# Revit family: Chaine de traitement par Absorption (support au sol) - AD5130
name_source: partatom
category: Equipement spécialisé
revit_build: Autodesk Revit 2018 (Build: 20170223_1515(x64)
units: mm (PartAtom-declared; Revit-internal decimal feet)

## family parameters
Basée sur le plan de construction = Non
Cote de connecteur circulaire = Utiliser le diamètre
Couper avec des vides une fois chargée = Non
Partagée = Non
Point de calcul de pièce = Non
Toujours verticalement = Oui
Type d'élément = Normal

## types (1)
- SEC 7 HC - AD 5130
    COS_PHI = 0.9
    DEBIT_ENTREE_AIR = 129.0 m³/h
    DEBIT_SORTIE_AIR = 129.0 m³/h
    DESCR_ALIM_X = Alimentation X ; ID 3G1mm² ;
    DESCR_ENTREE_AIR = Entrée Air ; 129 m3/h à 10 bar ; ID G 3/4" ;
    DESCR_SORTIE_AIR = Sortie Air ; 129 m3/h à 10 bar ; ID G 1/2" ;
    DIAM_ENTREE_AIR = 20 mm  [stored 0.0656168 ft]
    DIAM_SORTIE_AIR = 15 mm  [stored 0.0492126 ft]
    Diametre_Percement_1 = 11 mm  [stored 0.0360892 ft]
    Diametre_Percement_2 = 14 mm  [stored 0.0459318 ft]
    Diametre_Percement_3 = 25 mm  [stored 0.082021 ft]
    Entraxe_Horizontal_Percement_1 = 410 mm  [stored 1.34514 ft]
    Entraxe_Horizontal_Percement_2 = 410 mm  [stored 1.34514 ft]
    Entraxe_Rouleau = 313 mm  [stored 1.0269 ft]
    Entraxe_Vertical_Percement_1 = 400 mm  [stored 1.31234 ft]
    Entraxe_Vertical_Percement_2 = 150 mm
    FREQUENCE = 50 Hz
    Fabricant = MIL'S
    HAUTEUR = 1570 mm
    Hauteur_Boitier_Commande = 1050 mm
    Hauteur_Detente = 1470 mm
    Hauteur_Filtres = 800 mm  [stored 2.62467 ft]
    Hauteur_Rouleau = 20 mm  [stored 0.0656168 ft]
    Hauteur_Support = 1570 mm
    Hauteur_Vidange = 50 mm  [stored 0.164042 ft]
    LARGEUR = 460 mm  [stored 1.50919 ft]
    LONGUEUR = 250 mm  [stored 0.82021 ft]
    Largeur_Support = 460 mm  [stored 1.50919 ft]
    Lien espace client = https://www.mils.fr
    Longueur_Rouleau = 1480 mm  [stored 4.85564 ft]
    Modèle = SEC HC - AD 5130
    NBR_POLES = 1
    NEUTRE = Oui
    POIDS(Kg) = 100 mm  [stored 0.328084 ft]
    PUISS_APPARENTE_X = 167 VA
    PUISS_ELECT_X = 0 kW
    Profondeur_Support = 250 mm  [stored 0.82021 ft]
    TENSION_ALIM = 230 V
    TERRE = Oui

note: [stored X ft] marks values corroborated as IEEE doubles in the binary element streams (Revit-internal decimal feet)
